# Revit family: VP-3-MAF
name_source: partatom
category: Lighting Fixtures
units: mm (PartAtom-declared; Revit-internal decimal feet)

## family parameters
Cut with Voids When Loaded = No
Host = Face
Light Source = No
OmniClass Number = 23.80.70.11.14.17
OmniClass Title = Direct/Indirect
Part Type = Normal
Room Calculation Point = No
Round Connector Dimension = Use Diameter
Shared = Yes

## types (1)
- VP-3-MAF
    Apparent Load = 423 VA
    Assembly Code = D5020200
    Brand = Beacon
    CRI = 70
    Certification = UL
    Cool Grey = Cool Grey
    Default Elevation = 48 "
    Description = The Viper is an extremely versatile area/site luminaire which blends design, performance, and technology for a variety of applications.
    Features = Featuring two different optical technologies, Micro Strike and Strike Optics, which provide the best distribution patterns for retrofit or new construction
Vibration rated for high vibration applications including bridges and overpasses
Control options including photo control, occupancy sensing, NX Lighting Controls, wiSCAPE and 7-Pin with networked controls
Mounting options include: Arm, Universal Arm, Adjustable Arm, Mast Arm, Decorative Arm, Knuckle, Trunnion, Wall
Distribution options include: Auto Front Row, Type 2, Type 3, Type 4 Forward, Type 4 Wide, Type 5 Narrow, Type 5 Medium, Type 5 Wide, Type 5 Rectangular, Corner Optic, and Tennis Court
    Finish = Arctic White
    Glass = Glass
    Grey = Grey
    Lamp = LED
    Light Output = 30846 cd/m²
    Load Classification = Lighting
    Manufacturer = Current Lighting
    Matt Black = Matt Black
    Matt Grey = MATT GREY
    Matt White = Matt White
    Model = VP-3-MAF
    Name = Viper Area Size 3
    Power Factor = 0.9
    Product Documentation Link = https://cdn.currentlighting.com
    Product Page URL = https://www.currentlighting.com
    Type Comments = Lighting Fixture
    URL = https://www.currentlighting.com
    Voltage = 120 V
    Warranty = Five year warranty
    Wattage Comments = 423 W

## geometry (parser evidence)
native form markers: Blend x4, Sweep x5
no freeform markers — native parametric forms only
